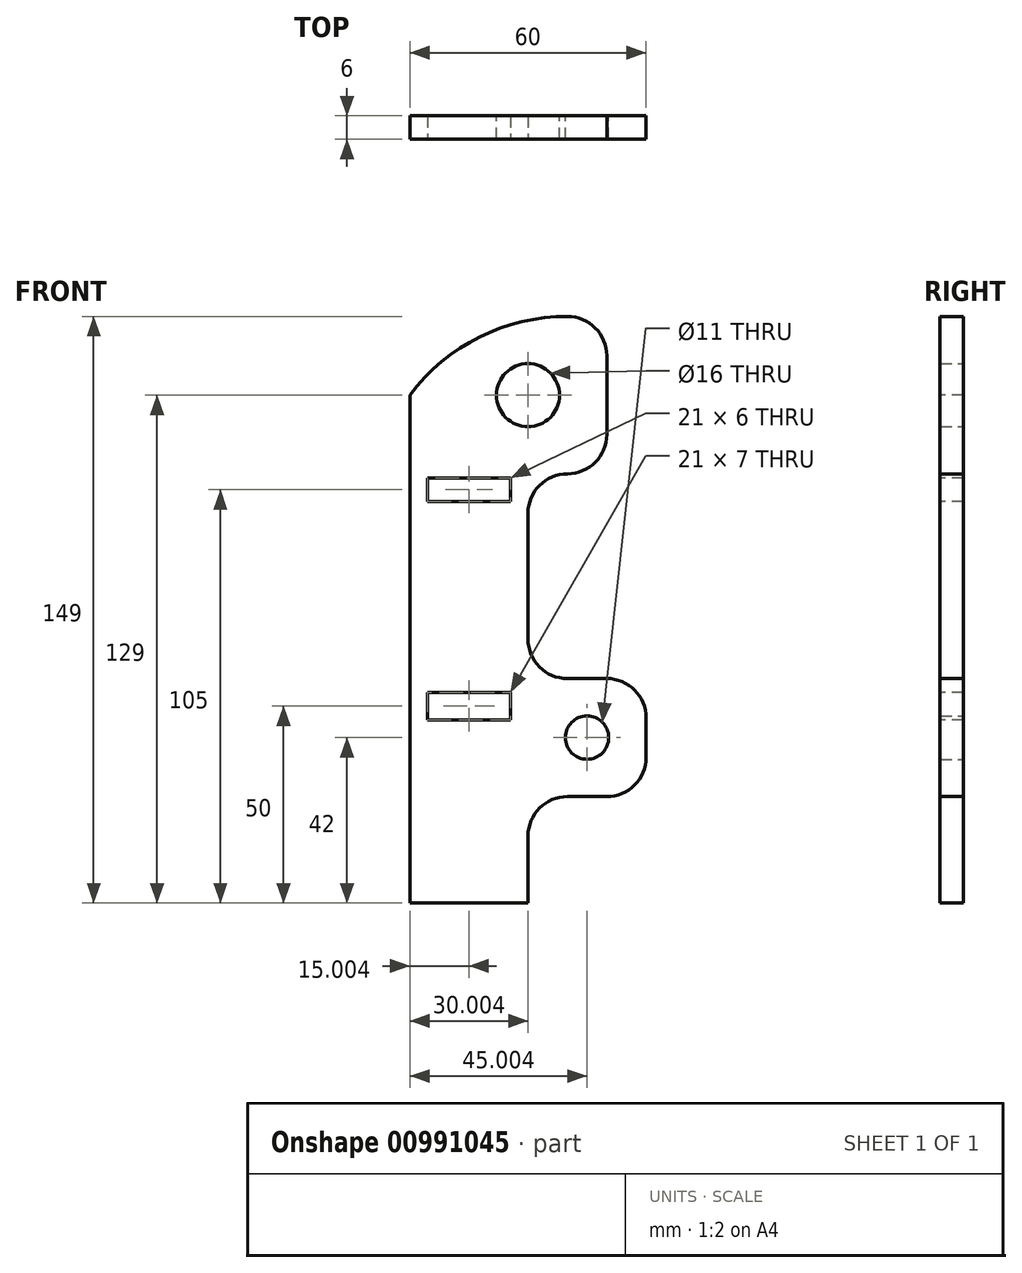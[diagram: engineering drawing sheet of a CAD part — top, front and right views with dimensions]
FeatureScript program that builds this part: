
annotation { "Feature Type Name" : "Feature", "Feature Type Description" : "" }
export const myFeature = defineFeature(function(context is Context, id is Id, definition is map)
    precondition{}
    {
        {
            var Q0;
            Q0=qCreatedBy(makeId("Front.planeOp"),FACE);
            var sketch = newSketch(context, id + "F0", { "sketchPlane" : qUnion([Q0])});
            skLineSegment(sketch, "E0.top", {"start": v(-59.44, -101.5) * mm, "end": v(-19.44, -101.5) * mm});
            skLineSegment(sketch, "E0.left", {"start": v(-59.44, 6.79) * mm, "end": v(-59.44, -101.5) * mm});
            skLineSegment(sketch, "E1", {"start": v(-59.44, -101.5) * mm, "end": v(-19.44, -101.5) * mm, "construction": true});
            skLineSegment(sketch, "E2", {"start": v(-4.44, -101.5) * mm, "end": v(-4.44, -53.5) * mm, "construction": true});
            skCircle(sketch, "E3", {"center": v(-4.44, -53.5) * mm, "radius": 5.5 * mm});
            skLineSegment(sketch, "E4", {"start": v(-4.44, -38.5) * mm, "end": v(-9.44, -38.5) * mm});
            skLineSegment(sketch, "E5", {"start": v(-19.44, -101.5) * mm, "end": v(-19.44, 33.5) * mm, "construction": true});
            skCircle(sketch, "E6", {"center": v(-19.44, 33.5) * mm, "radius": 8 * mm});
            skLineSegment(sketch, "E7", {"start": v(-19.44, 33.5) * mm, "end": v(0.56, 33.5) * mm, "construction": true});
            skLineSegment(sketch, "E8", {"start": v(0.56, 33.5) * mm, "end": v(0.56, 43.5) * mm});
            skLineSegment(sketch, "E9", {"start": v(0.56, 33.5) * mm, "end": v(0.56, 23.5) * mm});
            skLineSegment(sketch, "E10", {"start": v(-4.44, -53.5) * mm, "end": v(10.56, -53.5) * mm, "construction": true});
            skLineSegment(sketch, "E11", {"start": v(10.56, -53.5) * mm, "end": v(10.56, -48.5) * mm});
            skLineSegment(sketch, "E12", {"start": v(0.56, -38.5) * mm, "end": v(-4.44, -38.5) * mm});
            skLineSegment(sketch, "E13", {"start": v(-19.44, -28.5) * mm, "end": v(-19.44, 3.5) * mm});
            skLineSegment(sketch, "E14", {"start": v(-9.44, 13.5) * mm, "end": v(-9.44, 13.5) * mm});
            skLineSegment(sketch, "E15", {"start": v(10.56, -53.5) * mm, "end": v(10.56, -58.5) * mm});
            skLineSegment(sketch, "E16", {"start": v(0.56, -68.5) * mm, "end": v(-9.44, -68.5) * mm});
            skLineSegment(sketch, "E17", {"start": v(-19.44, -78.5) * mm, "end": v(-19.44, -101.5) * mm});
            skPoint(sketch, "E18.visualSharp", {"position": v(10.56, -68.5) * mm});
            skArc(sketch, "E18.filletArc", {"start": v(0.56, -68.5) * mm, "mid": v(7.63, -65.56) * mm, "end": v(10.56, -58.5) * mm});
            skPoint(sketch, "E19.visualSharp", {"position": v(10.56, -38.5) * mm});
            skArc(sketch, "E19.filletArc", {"start": v(10.56, -48.5) * mm, "mid": v(7.63, -41.42) * mm, "end": v(0.56, -38.5) * mm});
            skPoint(sketch, "E20.visualSharp", {"position": v(-19.44, -38.5) * mm});
            skArc(sketch, "E20.filletArc", {"start": v(-19.44, -28.5) * mm, "mid": v(-16.5, -35.56) * mm, "end": v(-9.44, -38.5) * mm});
            skPoint(sketch, "E21.visualSharp", {"position": v(-19.44, -68.5) * mm});
            skArc(sketch, "E21.filletArc", {"start": v(-9.44, -68.5) * mm, "mid": v(-16.5, -71.42) * mm, "end": v(-19.44, -78.5) * mm});
            skPoint(sketch, "E22.visualSharp", {"position": v(-19.44, 13.5) * mm});
            skArc(sketch, "E22.filletArc", {"start": v(-9.44, 13.5) * mm, "mid": v(-16.5, 10.58) * mm, "end": v(-19.44, 3.5) * mm});
            skPoint(sketch, "E23.visualSharp", {"position": v(0.56, 13.5) * mm});
            skArc(sketch, "E23.filletArc", {"start": v(-9.44, 13.5) * mm, "mid": v(-2.37, 16.44) * mm, "end": v(0.56, 23.5) * mm});
            skPoint(sketch, "E24.visualSharp", {"position": v(0.56, 53.5) * mm});
            skArc(sketch, "E24.filletArc", {"start": v(0.56, 43.5) * mm, "mid": v(-2.37, 50.58) * mm, "end": v(-9.44, 53.5) * mm});
            skPoint(sketch, "E25.visualSharp", {"position": v(-59.44, 53.5) * mm});
            skArc(sketch, "E26", {"start": v(-9.44, 53.5) * mm, "mid": v(-46.05, 37.61) * mm, "end": v(-59.44, 0) * mm});
            skSolve(sketch);
        }
        {
            var Q0;
            {var subQ0=sQuery(id+"F0.wireOp",EDGE,"E0.top");Q0=makeQuery(id+"F0.imprint","IMPRINT",FACE,{"disambiguationData":[TD([[makeQuery(id+"F0.imprint","IMPRINT",EDGE,{"derivedFrom":subQ0}),1.0]])]});}
            extrude(context, id + "F1", {"entities" : qUnion([Q0]), "depth" : 6 * mm, "offsetDistance" : 25 * mm});
        }
        {
            var Q0;
            Q0=makeQuery(id+"F1.opExtrude","CAP_FACE",FACE,{"disambiguationData":[OSD([sQuery(id+"F0.wireOp",EDGE,"E0.top"),sQuery(id+"F0.wireOp",EDGE,"E0.left"),sQuery(id+"F0.wireOp",EDGE,"E3"),sQuery(id+"F0.wireOp",EDGE,"E4"),sQuery(id+"F0.wireOp",EDGE,"E6"),sQuery(id+"F0.wireOp",EDGE,"E8"),sQuery(id+"F0.wireOp",EDGE,"E9"),sQuery(id+"F0.wireOp",EDGE,"E11"),sQuery(id+"F0.wireOp",EDGE,"E12"),sQuery(id+"F0.wireOp",EDGE,"E13"),sQuery(id+"F0.wireOp",EDGE,"E15"),sQuery(id+"F0.wireOp",EDGE,"E16"),sQuery(id+"F0.wireOp",EDGE,"E17"),sQuery(id+"F0.wireOp",EDGE,"E18.filletArc"),sQuery(id+"F0.wireOp",EDGE,"E19.filletArc"),sQuery(id+"F0.wireOp",EDGE,"E20.filletArc"),sQuery(id+"F0.wireOp",EDGE,"E21.filletArc"),sQuery(id+"F0.wireOp",EDGE,"E22.filletArc"),sQuery(id+"F0.wireOp",EDGE,"E23.filletArc"),sQuery(id+"F0.wireOp",EDGE,"E24.filletArc"),sQuery(id+"F0.wireOp",EDGE,"E26")])],"isStart":false});
            var sketch = newSketch(context, id + "F2", { "sketchPlane" : qUnion([Q0])});
            skLineSegment(sketch, "E27", {"start": v(-59.44, -101.5) * mm, "end": v(-49.44, -101.5) * mm});
            skLineSegment(sketch, "E28", {"start": v(-49.44, -101.5) * mm, "end": v(-49.44, 33.59) * mm});
            skSolve(sketch);
        }
        {
            var Q0;
            Q0=makeQuery(id+"F2.imprint","IMPRINT",FACE,{"disambiguationData":[TD([[makeQuery(id+"F2.imprint","IMPRINT",EDGE,{"derivedFrom":sQuery(id+"F2.wireOp",EDGE,"E27")}),1.0]])]});
            extrude(context, id + "F3", {"entities" : qUnion([Q0]), "operationType" : NewBodyOperationType.REMOVE, "oppositeDirection" : true, "depth" : 25 * mm, "offsetDistance" : 25 * mm});
        }
        {
            var Q0;
            Q0=makeQuery(id+"F1.opExtrude","CAP_FACE",FACE,{"disambiguationData":[OSD([sQuery(id+"F0.wireOp",EDGE,"E0.top"),sQuery(id+"F0.wireOp",EDGE,"E0.left"),sQuery(id+"F0.wireOp",EDGE,"E3"),sQuery(id+"F0.wireOp",EDGE,"E4"),sQuery(id+"F0.wireOp",EDGE,"E6"),sQuery(id+"F0.wireOp",EDGE,"E8"),sQuery(id+"F0.wireOp",EDGE,"E9"),sQuery(id+"F0.wireOp",EDGE,"E11"),sQuery(id+"F0.wireOp",EDGE,"E12"),sQuery(id+"F0.wireOp",EDGE,"E13"),sQuery(id+"F0.wireOp",EDGE,"E15"),sQuery(id+"F0.wireOp",EDGE,"E16"),sQuery(id+"F0.wireOp",EDGE,"E17"),sQuery(id+"F0.wireOp",EDGE,"E18.filletArc"),sQuery(id+"F0.wireOp",EDGE,"E19.filletArc"),sQuery(id+"F0.wireOp",EDGE,"E20.filletArc"),sQuery(id+"F0.wireOp",EDGE,"E21.filletArc"),sQuery(id+"F0.wireOp",EDGE,"E22.filletArc"),sQuery(id+"F0.wireOp",EDGE,"E23.filletArc"),sQuery(id+"F0.wireOp",EDGE,"E24.filletArc"),sQuery(id+"F0.wireOp",EDGE,"E26")])],"isStart":false});
            var sketch = newSketch(context, id + "F4", { "sketchPlane" : qUnion([Q0])});
            skLineSegment(sketch, "E29", {"start": v(-49.44, -101.5) * mm, "end": v(-49.44, -95.5) * mm});
            skLineSegment(sketch, "E30", {"start": v(-49.44, -95.5) * mm, "end": v(-19.44, -95.5) * mm});
            skSolve(sketch);
        }
        {
            var Q0;
            Q0=makeQuery(id+"F4.imprint","IMPRINT",FACE,{"disambiguationData":[TD([[makeQuery(id+"F4.imprint","IMPRINT",EDGE,{"derivedFrom":sQuery(id+"F4.wireOp",EDGE,"E29")}),-1.0]])]});
            extrude(context, id + "F5", {"entities" : qUnion([Q0]), "operationType" : NewBodyOperationType.REMOVE, "oppositeDirection" : true, "depth" : 25 * mm, "offsetDistance" : 25 * mm});
        }
        {
            var Q0;
            Q0=makeQuery(id+"F1.opExtrude","CAP_FACE",FACE,{"disambiguationData":[OSD([sQuery(id+"F0.wireOp",EDGE,"E0.top"),sQuery(id+"F0.wireOp",EDGE,"E0.left"),sQuery(id+"F0.wireOp",EDGE,"E3"),sQuery(id+"F0.wireOp",EDGE,"E4"),sQuery(id+"F0.wireOp",EDGE,"E6"),sQuery(id+"F0.wireOp",EDGE,"E8"),sQuery(id+"F0.wireOp",EDGE,"E9"),sQuery(id+"F0.wireOp",EDGE,"E11"),sQuery(id+"F0.wireOp",EDGE,"E12"),sQuery(id+"F0.wireOp",EDGE,"E13"),sQuery(id+"F0.wireOp",EDGE,"E15"),sQuery(id+"F0.wireOp",EDGE,"E16"),sQuery(id+"F0.wireOp",EDGE,"E17"),sQuery(id+"F0.wireOp",EDGE,"E18.filletArc"),sQuery(id+"F0.wireOp",EDGE,"E19.filletArc"),sQuery(id+"F0.wireOp",EDGE,"E20.filletArc"),sQuery(id+"F0.wireOp",EDGE,"E21.filletArc"),sQuery(id+"F0.wireOp",EDGE,"E22.filletArc"),sQuery(id+"F0.wireOp",EDGE,"E23.filletArc"),sQuery(id+"F0.wireOp",EDGE,"E24.filletArc"),sQuery(id+"F0.wireOp",EDGE,"E26")])],"isStart":false});
            var sketch = newSketch(context, id + "F6", { "sketchPlane" : qUnion([Q0])});
            skLineSegment(sketch, "E31", {"start": v(-34.44, -95.5) * mm, "end": v(-34.44, -45.5) * mm, "construction": true});
            skLineSegment(sketch, "E32", {"start": v(-34.44, -45.5) * mm, "end": v(-34.44, 9.5) * mm, "construction": true});
            skLineSegment(sketch, "E33.bottom", {"start": v(-23.94, -49) * mm, "end": v(-44.94, -49) * mm});
            skLineSegment(sketch, "E33.top", {"start": v(-23.94, -42) * mm, "end": v(-44.94, -42) * mm});
            skLineSegment(sketch, "E33.left", {"start": v(-23.94, -49) * mm, "end": v(-23.94, -42) * mm});
            skLineSegment(sketch, "E33.right", {"start": v(-44.94, -49) * mm, "end": v(-44.94, -42) * mm});
            skPoint(sketch, "E33.middle", {"position": v(-34.44, -45.5) * mm});
            skLineSegment(sketch, "E34.bottom", {"start": v(-23.94, 6.5) * mm, "end": v(-44.94, 6.5) * mm});
            skLineSegment(sketch, "E34.top", {"start": v(-23.94, 12.5) * mm, "end": v(-44.94, 12.5) * mm});
            skLineSegment(sketch, "E34.left", {"start": v(-23.94, 6.5) * mm, "end": v(-23.94, 12.5) * mm});
            skLineSegment(sketch, "E34.right", {"start": v(-44.94, 6.5) * mm, "end": v(-44.94, 12.5) * mm});
            skPoint(sketch, "E34.middle", {"position": v(-34.44, 9.5) * mm});
            skSolve(sketch);
        }
        {
            var Q0;
            Q0 = qSketchRegion(id + "F6", true);
            extrude(context, id + "F7", {"entities" : qUnion([Q0]), "operationType" : NewBodyOperationType.REMOVE, "oppositeDirection" : true, "depth" : 25 * mm, "offsetDistance" : 25 * mm});
        }
    });
